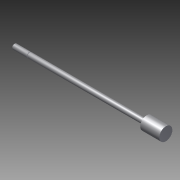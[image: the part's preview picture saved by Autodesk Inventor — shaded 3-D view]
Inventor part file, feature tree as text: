
AUTODESK INVENTOR PART (.ipt)
format: ipt  version: 2012 (Build 160160000, 160)  size: 127,488 bytes
history: native  units: in
note: dims shown in document units (in); Inventor stores cm internally (conversion verified against a paired STEP export)
features: other x84, revolve x3, sketch x3
ambient origin geometry x8: Origin, YZ Plane, XZ Plane, XY Plane, X Axis, Y Axis, Z Axis, Center Point
bodies: Solid1 (feature_tree)
feature tree (90):
  revolve  "Revolution1"  Angle=360.0deg
  revolve  "Revolution2"  [1 undecoded]
  revolve  "Revolution3"  [1 undecoded]
  other  "rod_cp_XY"
  other  "rod_cp_YZ"
  other  "rod_cp_ZX"
  other  "rod_cp_X"
  other  "rod_cp_Y"
  other  "rod_cp_Z"
  other  "rod_cp_Center"
  other  "to_rod_clevis_XY"
  other  "to_rod_clevis_YZ"
  other  "to_rod_clevis_ZX"
  other  "to_rod_clevis_X"
  other  "to_rod_clevis_Y"
  other  "to_rod_clevis_Z"
  other  "to_rod_clevis_Center"
  other  "rl2_XY"
  other  "rl2_YZ"
  other  "rl2_ZX"
  other  "rl2_X"
  other  "rl2_Y"
  other  "rl2_Z"
  other  "rl2_Center"
  other  "rl1_XY"
  other  "rl1_YZ"
  other  "rl1_ZX"
  other  "rl1_X"
  other  "rl1_Y"
  other  "rl1_Z"
  other  "rl1_Center"
  other  "thd1_XY"
  other  "thd1_YZ"
  other  "thd1_ZX"
  other  "thd1_X"
  other  "thd1_Y"
  other  "thd1_Z"
  other  "thd1_Center"
  other  "thd2_XY"
  other  "thd2_YZ"
  other  "thd2_ZX"
  other  "thd2_X"
  other  "thd2_Y"
  other  "thd2_Z"
  other  "thd2_Center"
  other  "dia1_XY"
  other  "dia1_YZ"
  other  "dia1_ZX"
  other  "dia1_X"
  other  "dia1_Y"
  other  "dia1_Z"
  other  "dia1_Center"
  other  "dia2_XY"
  other  "dia2_YZ"
  other  "dia2_ZX"
  other  "dia2_X"
  other  "dia2_Y"
  other  "dia2_Z"
  other  "dia2_Center"
  other  "dia1r_XY"
  other  "dia1r_YZ"
  other  "dia1r_ZX"
  other  "dia1r_X"
  other  "dia1r_Y"
  other  "dia1r_Z"
  other  "dia1r_Center"
  other  "dia2r_XY"
  other  "dia2r_YZ"
  other  "dia2r_ZX"
  other  "dia2r_X"
  other  "dia2r_Y"
  other  "dia2r_Z"
  other  "dia2r_Center"
  other  "dia12_XY"
  other  "dia12_YZ"
  other  "dia12_ZX"
  other  "dia12_X"
  other  "dia12_Y"
  other  "dia12_Z"
  other  "dia12_Center"
  other  "dia22_XY"
  other  "dia22_YZ"
  other  "dia22_ZX"
  other  "dia22_X"
  other  "dia22_Y"
  other  "dia22_Z"
  other  "dia22_Center"
  sketch  "Sketch_1"  dims[d0=360.0deg d1=360.0deg]
  sketch  "Sketch_2"  dims[d2=360.0deg]
  sketch  "Sketch_30"
note: 2 required parameter values undecoded (feature->parameter linkage not recoverable at this tier; creation-order binding heuristic only, values carry confidence <= 0.55)
